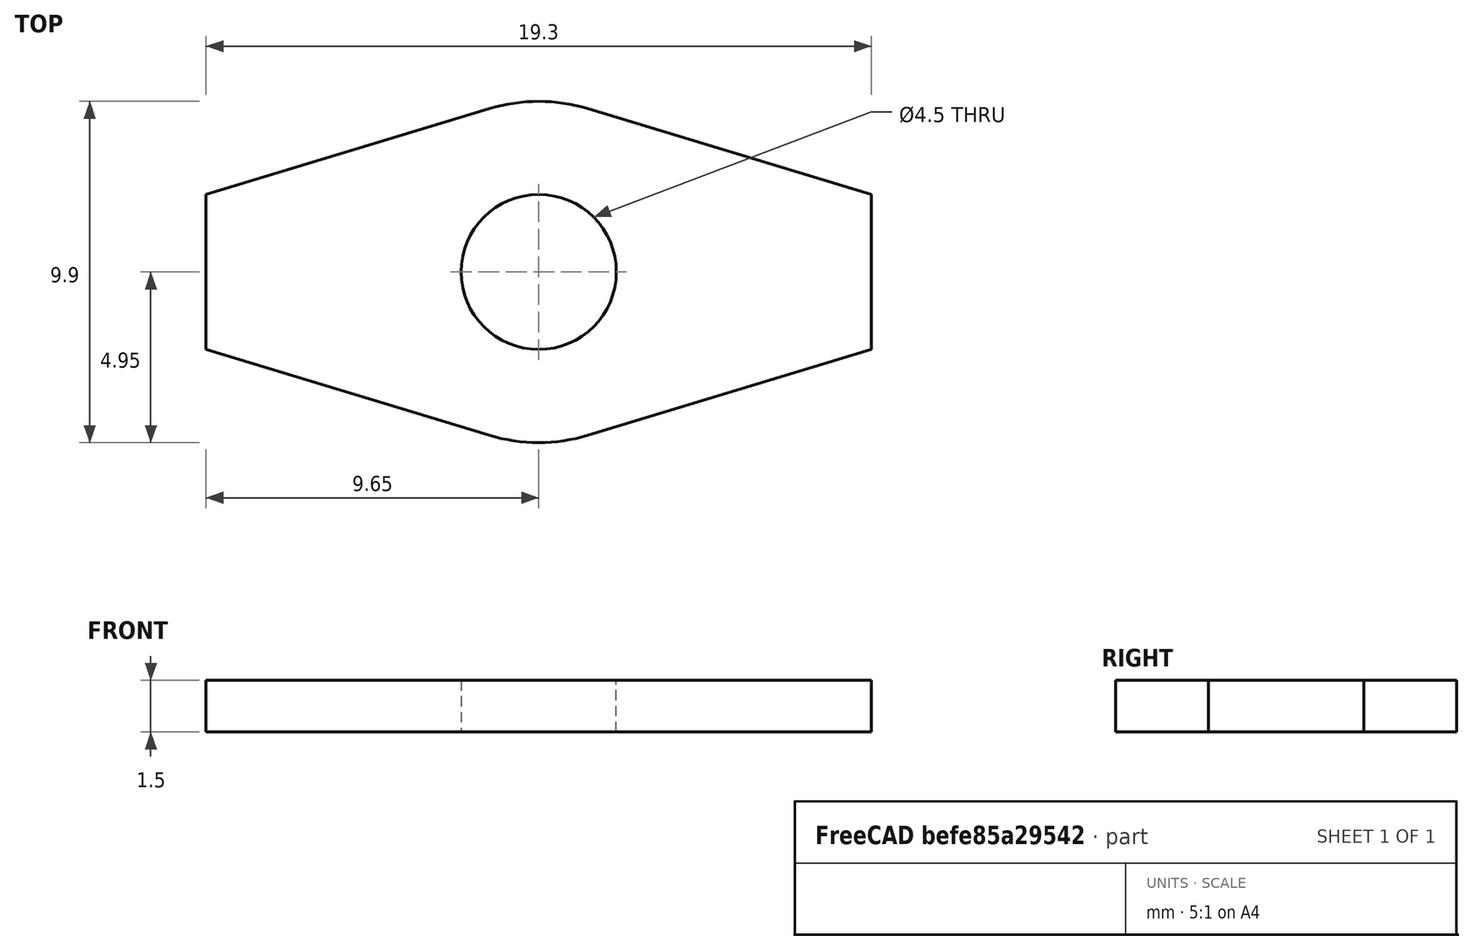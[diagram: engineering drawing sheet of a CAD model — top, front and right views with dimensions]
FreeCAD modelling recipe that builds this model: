
FCSTD DOCUMENT  (FreeCAD 0.19R17331 (Git))
Label: jeringa1mL
License: All rights reserved
LicenseURL: http://en.wikipedia.org/wiki/All_rights_reserved
objects: Sketcher::SketchObject×1, PartDesign::Pad×1, PartDesign::Body×1
note: 4 computed .brp shape members not serialized (recipe doc carries the construction recipe); baked Part::Feature solids carry a one-line shape summary decoded from their .brp

FEATURE [Sketcher::SketchObject] Sketch
  MapMode = 5
  Support = -> [XY_Plane]
  sketch-geometry (21):
    g0: Circle CenterX=0 CenterY=0 CenterZ=0 NormalX=0 NormalY=0 NormalZ=1 AngleXU=0 Radius=2.25
    g1: LineSegment [constr] StartX=-9.65 StartY=-4.95 StartZ=0 EndX=9.65 EndY=-4.95 EndZ=0
    g2: LineSegment [constr] StartX=9.65 StartY=-4.95 StartZ=0 EndX=9.65 EndY=4.95 EndZ=0
    g3: LineSegment [constr] StartX=9.65 StartY=4.95 StartZ=0 EndX=-9.65 EndY=4.95 EndZ=0
    g4: LineSegment [constr] StartX=-9.65 StartY=4.95 StartZ=0 EndX=-9.65 EndY=-4.95 EndZ=0
    g5: ArcOfCircle CenterX=0 CenterY=0 CenterZ=0 NormalX=0 NormalY=0 NormalZ=1 AngleXU=0 Radius=4.95 StartAngle=1.27678 EndAngle=1.86481
    g6: ArcOfCircle CenterX=0 CenterY=0 CenterZ=0 NormalX=0 NormalY=0 NormalZ=1 AngleXU=0 Radius=4.95 StartAngle=4.41837 EndAngle=5.0064
    g7: LineSegment [constr] StartX=-1.4345 StartY=4.73758 StartZ=0 EndX=1.4345 EndY=4.73758 EndZ=0
    g8: LineSegment [constr] StartX=1.4345 StartY=4.73758 StartZ=0 EndX=1.4345 EndY=-4.73758 EndZ=0
    g9: LineSegment [constr] StartX=1.4345 StartY=-4.73758 StartZ=0 EndX=-1.4345 EndY=-4.73758 EndZ=0
    g10: LineSegment [constr] StartX=-1.4345 StartY=-4.73758 StartZ=0 EndX=-1.4345 EndY=4.73758 EndZ=0
    g11: LineSegment StartX=-9.65 StartY=2.25 StartZ=0 EndX=-9.65 EndY=-2.25 EndZ=0
    g12: LineSegment StartX=9.65 StartY=2.25 StartZ=0 EndX=9.65 EndY=-2.25 EndZ=0
    g13: LineSegment StartX=-9.65 StartY=2.25 StartZ=0 EndX=-1.4345 EndY=4.73758 EndZ=0
    g14: LineSegment StartX=-9.65 StartY=-2.25 StartZ=0 EndX=-1.4345 EndY=-4.73758 EndZ=0
    g15: LineSegment StartX=1.4345 StartY=-4.73758 StartZ=0 EndX=9.65 EndY=-2.25 EndZ=0
    g16: LineSegment StartX=1.4345 StartY=4.73758 StartZ=0 EndX=9.65 EndY=2.25 EndZ=0
    g17: LineSegment [constr] StartX=-9.65 StartY=2.25 StartZ=0 EndX=9.65 EndY=2.25 EndZ=0
    g18: LineSegment [constr] StartX=9.65 StartY=2.25 StartZ=0 EndX=9.65 EndY=-2.25 EndZ=0
    g19: LineSegment [constr] StartX=9.65 StartY=-2.25 StartZ=0 EndX=-9.65 EndY=-2.25 EndZ=0
    g20: LineSegment [constr] StartX=-9.65 StartY=-2.25 StartZ=0 EndX=-9.65 EndY=2.25 EndZ=0
  constraints (50):
    c: Coincident(g0,g-1)
    c: Coincident(g1,g2)
    c: Coincident(g2,g3)
    c: Coincident(g3,g4)
    c: Coincident(g4,g1)
    c: Horizontal(g1)
    c: Vertical(g2)
    c: Symmetric(g3,g2,g-2)
    c: Symmetric(g1,g3,g-1)
    c: DistanceY(g2,g2) = 9.9
    c: Diameter(g0) = 4.5
    c: DistanceX(g1,g1) = 19.3
    c: Coincident(g5,g0)
    c: Coincident(g6,g0)
    c: Coincident(g7,g8)
    c: Coincident(g8,g9)
    c: Coincident(g9,g10)
    c: Coincident(g10,g7)
    c: Horizontal(g7)
    c: Horizontal(g9)
    c: Vertical(g8)
    c: Coincident(g7,g5)
    c: Coincident(g8,g6)
    c: Coincident(g5,g7)
    c: Coincident(g6,g9)
    c: Tangent(g5,g3)
    c: Tangent(g6,g1)
    c: PointOnObject(g11,g4)
    c: PointOnObject(g11,g4)
    c: PointOnObject(g12,g2)
    c: Coincident(g13,g11)
    c: Coincident(g13,g5)
    c: Coincident(g14,g11)
    c: Coincident(g14,g6)
    c: Coincident(g15,g6)
    c: Coincident(g15,g12)
    c: Coincident(g16,g12)
    c: Equal(g11,g12)
    c: DistanceY(g12,g12) = 4.5
    c: Coincident(g17,g18)
    c: Coincident(g18,g19)
    c: Coincident(g19,g20)
    c: Coincident(g20,g17)
    c: Horizontal(g17)
    c: Coincident(g17,g11)
    c: Coincident(g18,g12)
    c: Coincident(g17,g12)
    c: Coincident(g19,g11)
    c: Symmetric(g12,g12,g-1)
    c: Tangent(g16,g5) = 1.5708
FEATURE [PartDesign::Pad] Pad
  Length = 1.5
  Length2 = 100
  Profile = -> Sketch
  Type = 0
FEATURE [PartDesign::Body] Body  label="topeJeringa1mL"
  Group = -> [Sketch,Pad]
  Origin = -> Origin
  Tip = -> Pad
